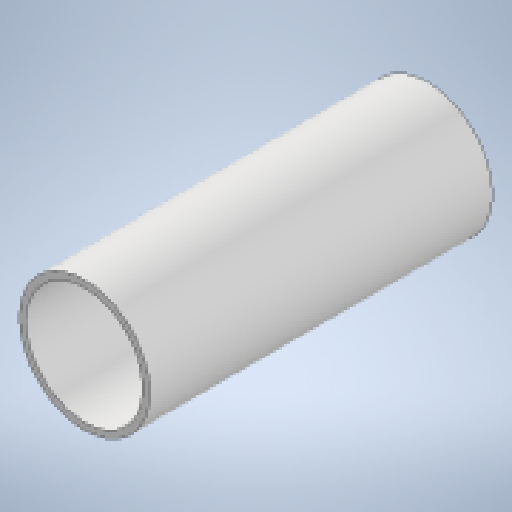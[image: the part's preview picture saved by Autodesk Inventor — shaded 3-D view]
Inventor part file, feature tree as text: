
AUTODESK INVENTOR PART (.ipt)
format: ipt  version: 2025.4 (Build 294407000, 407)  size: 142,336 bytes
history: native  units: mm
features: extrude x1, sketch x1
ambient origin geometry x8: Origin, YZ Plane, XZ Plane, XY Plane, X Axis, Y Axis, Z Axis, Center Point
bodies: Solid1 (feature_tree)
feature tree (2):
  extrude  "Extrusion1"  Depth=150.0mm
  sketch  "Sketch1"  dims[d0=57.0mm d1=3.0mm d2=150.0mm d3=0.0mm]
